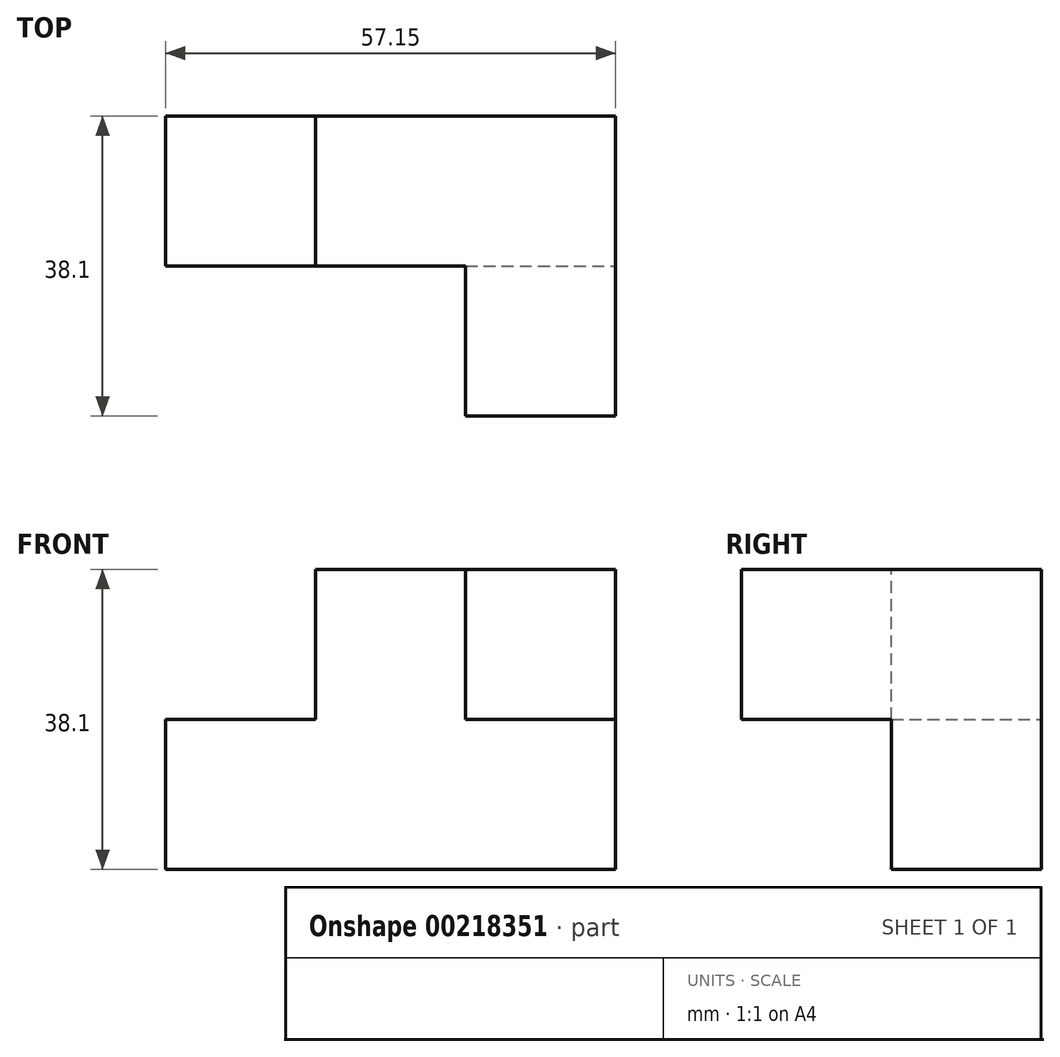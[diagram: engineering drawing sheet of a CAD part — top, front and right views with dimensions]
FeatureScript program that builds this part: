
annotation { "Feature Type Name" : "Feature", "Feature Type Description" : "" }
export const myFeature = defineFeature(function(context is Context, id is Id, definition is map)
    precondition{}
    {
        {
            var Q0;
            Q0=qCreatedBy(makeId("Front.planeOp"),FACE);
            var sketch = newSketch(context, id + "F0", { "sketchPlane" : qUnion([Q0])});
            skLineSegment(sketch, "E0.top", {"start": v(0, 0) * mm, "end": v(4.7, 0) * mm});
            skLineSegment(sketch, "E1.bottom", {"start": v(4.7, 0) * mm, "end": v(-14.36, 0) * mm});
            skLineSegment(sketch, "E1.top", {"start": v(4.7, 19.05) * mm, "end": v(-14.36, 19.05) * mm});
            skLineSegment(sketch, "E1.left", {"start": v(4.7, 0) * mm, "end": v(4.7, 19.05) * mm});
            skLineSegment(sketch, "E1.right", {"start": v(-14.36, 0) * mm, "end": v(-14.36, 19.05) * mm});
            skLineSegment(sketch, "E2.top", {"start": v(4.7, -19.05) * mm, "end": v(-14.36, -19.05) * mm});
            skLineSegment(sketch, "E2.left", {"start": v(4.7, 0) * mm, "end": v(4.7, -19.05) * mm});
            skLineSegment(sketch, "E2.right", {"start": v(-14.36, 0) * mm, "end": v(-14.36, -19.05) * mm});
            skLineSegment(sketch, "E3.bottom", {"start": v(-14.36, -19.05) * mm, "end": v(-33.4, -19.05) * mm});
            skLineSegment(sketch, "E3.top", {"start": v(-14.36, 0) * mm, "end": v(-33.4, 0) * mm});
            skLineSegment(sketch, "E3.left", {"start": v(-14.36, -19.05) * mm, "end": v(-14.36, 0) * mm});
            skLineSegment(sketch, "E3.right", {"start": v(-33.4, -19.05) * mm, "end": v(-33.4, 0) * mm});
            skLineSegment(sketch, "E4.bottom", {"start": v(4.7, 0) * mm, "end": v(23.74, 0) * mm});
            skLineSegment(sketch, "E4.top", {"start": v(4.7, -19.05) * mm, "end": v(23.74, -19.05) * mm});
            skLineSegment(sketch, "E4.right", {"start": v(23.74, 0) * mm, "end": v(23.74, -19.05) * mm});
            skLineSegment(sketch, "E5.bottom", {"start": v(4.7, 19.05) * mm, "end": v(23.74, 19.05) * mm});
            skLineSegment(sketch, "E5.left", {"start": v(4.7, 19.05) * mm, "end": v(4.7, 0) * mm});
            skLineSegment(sketch, "E5.right", {"start": v(23.74, 19.05) * mm, "end": v(23.74, 0) * mm});
            skSolve(sketch);
        }
        {
            var Q0;
            Q0=makeQuery(id+"F0.imprint","IMPRINT",FACE,{"disambiguationData":[TD([[makeQuery(id+"F0.imprint","IMPRINT",EDGE,{"derivedFrom":sQuery(id+"F0.wireOp",EDGE,"E5.bottom")}),-1.0]])]});
            extrude(context, id + "F1", {"entities" : qUnion([Q0]), "depth" : 38.1 * mm});
        }
        {
            var Q0;
            Q0 = qSketchRegion(id + "F0", true);
            extrude(context, id + "F2", {"entities" : qUnion([Q0]), "operationType" : NewBodyOperationType.ADD, "depth" : 19.05 * mm});
        }
    });
